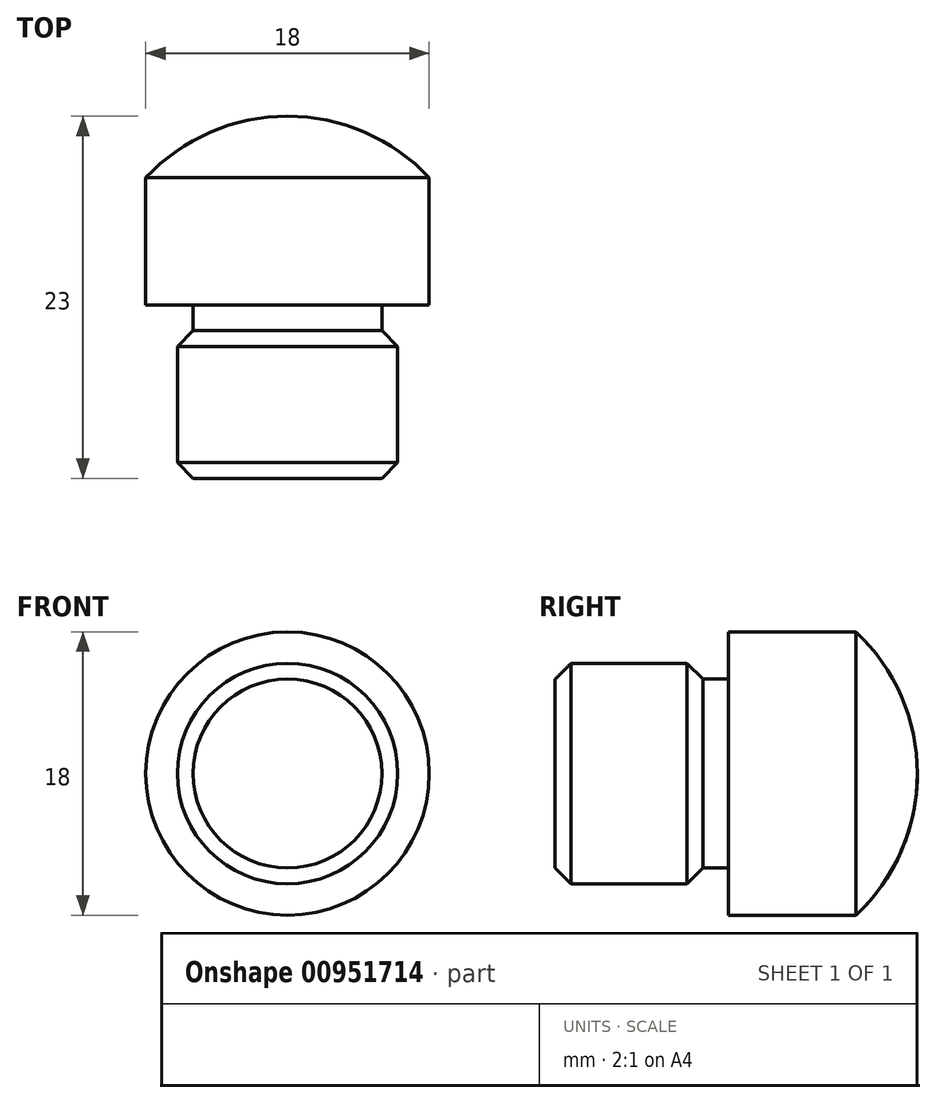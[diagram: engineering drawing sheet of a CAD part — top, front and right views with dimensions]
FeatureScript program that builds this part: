
annotation { "Feature Type Name" : "Feature", "Feature Type Description" : "" }
export const myFeature = defineFeature(function(context is Context, id is Id, definition is map)
    precondition{}
    {
        {
            var Q0;
            Q0=qCreatedBy(makeId("Right.planeOp"),FACE);
            var sketch = newSketch(context, id + "F0", { "sketchPlane" : qUnion([Q0])});
            skLineSegment(sketch, "E0", {"start": v(0, 0) * mm, "end": v(19.1, 0) * mm});
            skLineSegment(sketch, "E1", {"start": v(19.1, 0) * mm, "end": v(19.1, 9) * mm});
            skLineSegment(sketch, "E2", {"start": v(19.1, 9) * mm, "end": v(11, 9) * mm});
            skLineSegment(sketch, "E3", {"start": v(11, 9) * mm, "end": v(11, 7) * mm});
            skLineSegment(sketch, "E4", {"start": v(9.38, 7) * mm, "end": v(0, 7) * mm});
            skLineSegment(sketch, "E5", {"start": v(0, 7) * mm, "end": v(0, 0) * mm});
            skArc(sketch, "E6", {"start": v(23, 0) * mm, "mid": v(21.98, 4.9) * mm, "end": v(19.1, 9) * mm});
            skLineSegment(sketch, "E7", {"start": v(11, 7) * mm, "end": v(11, 0) * mm});
            skLineSegment(sketch, "E8", {"start": v(9.38, 7) * mm, "end": v(9.38, 0) * mm});
            skLineSegment(sketch, "E9", {"start": v(9.38, 6) * mm, "end": v(11, 6) * mm});
            skLineSegment(sketch, "E10", {"start": v(19.1, 0) * mm, "end": v(23, 0) * mm});
            skPoint(sketch, "E11.orphan", {"position": v(19.1, -9) * mm});
            skSolve(sketch);
        }
        {
            var Q0;
            {var subQ1=sQuery(id+"F0.wireOp",EDGE,"E1");Q0=makeQuery(id+"F0.imprint","IMPRINT",FACE,{"disambiguationData":[TD([[makeQuery(id+"F0.imprint","IMPRINT",EDGE,{"derivedFrom":subQ1}),1.0]])]});}
            var Q1;
            Q1=makeQuery(id+"F0.imprint","IMPRINT",FACE,{"disambiguationData":[TD([[makeQuery(id+"F0.imprint","IMPRINT",EDGE,{"derivedFrom":sQuery(id+"F0.wireOp",EDGE,"E1")}),-1.0]])]});
            var Q2;
            {var subQ2=sQuery(id+"F0.wireOp",EDGE,"E4");Q2=makeQuery(id+"F0.imprint","IMPRINT",FACE,{"disambiguationData":[TD([[makeQuery(id+"F0.imprint","IMPRINT",EDGE,{"derivedFrom":subQ2}),1.0]])]});}
            var Q3;
            {var subQ5=sQuery(id+"F0.wireOp",EDGE,"E9");Q3=makeQuery(id+"F0.imprint","IMPRINT",FACE,{"disambiguationData":[TD([[makeQuery(id+"F0.imprint","IMPRINT",EDGE,{"derivedFrom":subQ5}),-1.0]])]});}
            var Q4;
            Q4=sQuery(id+"F0.wireOp",EDGE,"E0");
            revolve(context, id + "F1", {"surfaceOperationType" : NewSurfaceOperationType.NEW, "entities" : qUnion([Q0, Q1, Q2, Q3]), "axis" : qUnion([Q4]), "revolveType" : RevolveType.FULL});
        }
        {
            var Q0;
            Q0=makeQuery(id+"F1.opRevolve","SWEPT_EDGE",EDGE,{"disambiguationData":[OSD([sQuery(id+"F0.wireOp",EDGE,"E4"),sQuery(id+"F0.wireOp",EDGE,"E8")])]});
            var Q1;
            Q1=makeQuery(id+"F1.opRevolve","SWEPT_EDGE",EDGE,{"disambiguationData":[OSD([sQuery(id+"F0.wireOp",EDGE,"E4"),sQuery(id+"F0.wireOp",EDGE,"E5")])]});
            chamfer(context, id + "F2", {"entities" : qUnion([Q0, Q1]), "width" : 1 * mm, "tangentPropagation" : true});
        }
    });
